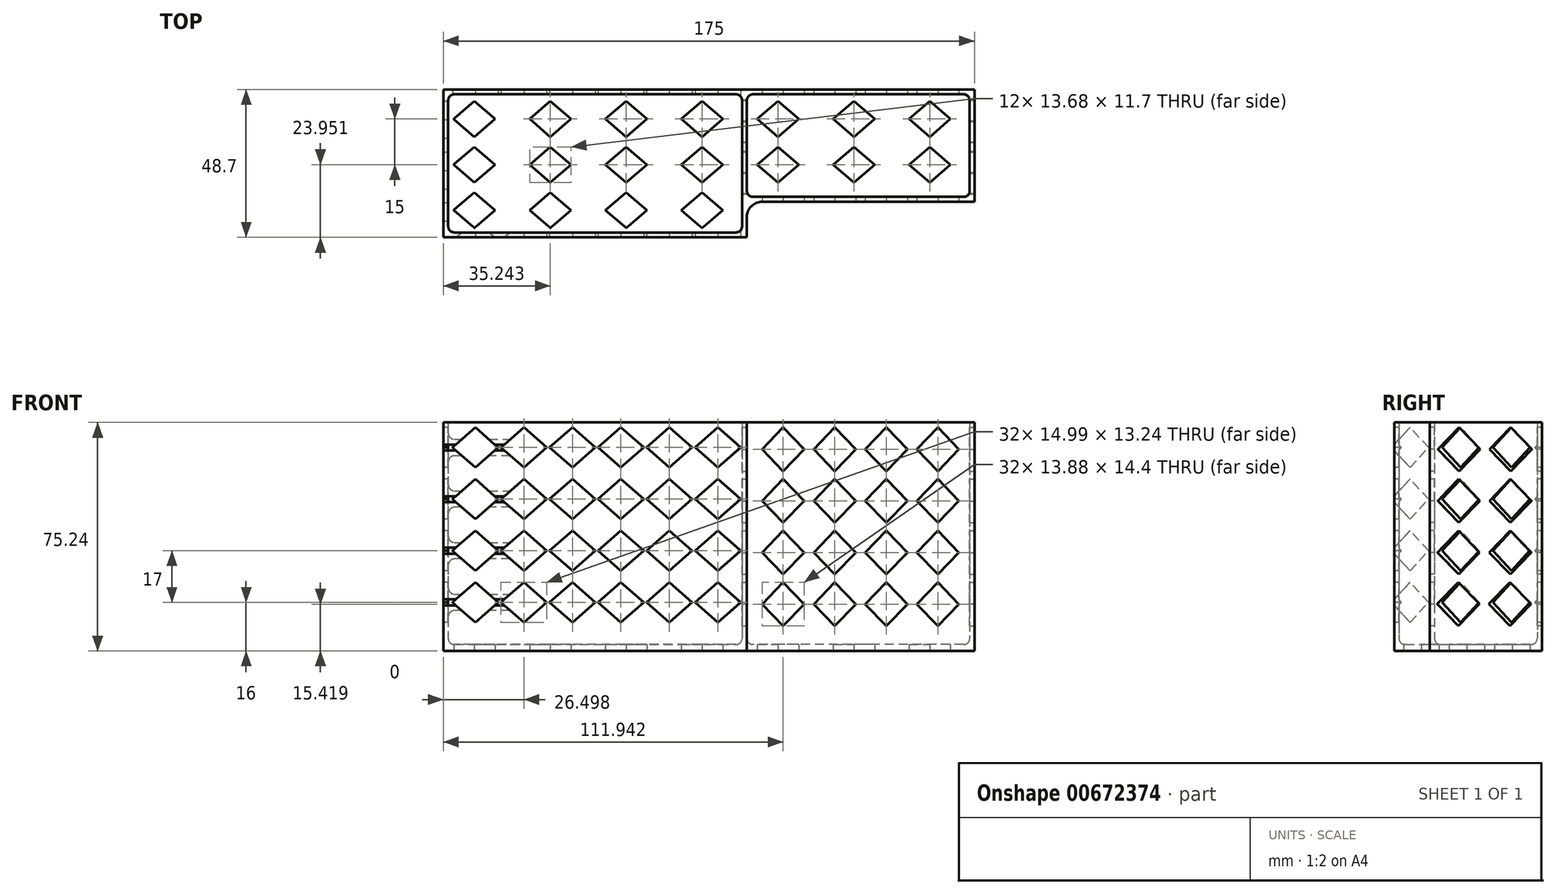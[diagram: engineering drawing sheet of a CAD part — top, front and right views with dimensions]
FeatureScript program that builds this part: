
annotation { "Feature Type Name" : "Feature", "Feature Type Description" : "" }
export const myFeature = defineFeature(function(context is Context, id is Id, definition is map)
    precondition{}
    {
        {
            var Q0;
            Q0=qCreatedBy(makeId("Top.planeOp"),FACE);
            var sketch = newSketch(context, id + "F0", { "sketchPlane" : qUnion([Q0])});
            skLineSegment(sketch, "E0.top", {"start": v(49.36, 40.94) * mm, "end": v(-50.64, 40.94) * mm});
            skPoint(sketch, "E0.middle", {"position": v(0, 0) * mm});
            skLineSegment(sketch, "E1", {"start": v(-49.04, -6.16) * mm, "end": v(47.76, -6.16) * mm});
            skLineSegment(sketch, "E2", {"start": v(-0.64, 40.94) * mm, "end": v(0.56, -22.16) * mm, "construction": true});
            skLineSegment(sketch, "E3.top", {"start": v(47.76, 39.34) * mm, "end": v(-49.04, 39.34) * mm});
            skPoint(sketch, "E3.middle", {"position": v(-0.2, 17.86) * mm});
            skLineSegment(sketch, "E4", {"start": v(47.76, 39.34) * mm, "end": v(47.76, -6.16) * mm});
            skLineSegment(sketch, "E5", {"start": v(-49.04, 39.34) * mm, "end": v(-49.04, -6.16) * mm});
            skLineSegment(sketch, "E6.bottom", {"start": v(49.36, 40.94) * mm, "end": v(124.36, 40.94) * mm});
            skLineSegment(sketch, "E6.top", {"start": v(49.36, 3.94) * mm, "end": v(124.36, 3.94) * mm});
            skLineSegment(sketch, "E6.right", {"start": v(124.36, 40.94) * mm, "end": v(124.36, 3.94) * mm});
            skPoint(sketch, "E7.orphan", {"position": v(-48.1, -7.76) * mm});
            skLineSegment(sketch, "E8", {"start": v(-50.64, -7.76) * mm, "end": v(49.36, -7.76) * mm});
            skLineSegment(sketch, "E9", {"start": v(-50.64, 40.94) * mm, "end": v(-50.64, -7.76) * mm});
            skLineSegment(sketch, "E10", {"start": v(49.36, 3.94) * mm, "end": v(49.36, -7.76) * mm});
            skLineSegment(sketch, "E11.top", {"start": v(49.36, 5.54) * mm, "end": v(122.76, 5.54) * mm});
            skLineSegment(sketch, "E11.right", {"start": v(122.76, 39.34) * mm, "end": v(122.76, 5.54) * mm});
            skPoint(sketch, "E12.orphan", {"position": v(-50.64, -6.16) * mm});
            skPoint(sketch, "E13.orphan", {"position": v(49.36, -6.16) * mm});
            skLineSegment(sketch, "E14", {"start": v(49.36, 39.34) * mm, "end": v(122.76, 39.34) * mm});
            skLineSegment(sketch, "E15", {"start": v(49.36, 39.34) * mm, "end": v(49.36, 5.54) * mm});
            skSolve(sketch);
        }
        {
            var Q0;
            Q0=makeQuery(id+"F0.imprint","IMPRINT",FACE,{"disambiguationData":[TD([[makeQuery(id+"F0.imprint","IMPRINT",EDGE,{"derivedFrom":sQuery(id+"F0.wireOp",EDGE,"E0.top")}),1.0]])]});
            extrude(context, id + "F1", {"entities" : qUnion([Q0]), "depth" : 130 * mm, "offsetDistance" : 25 * mm});
        }
        {
            var Q0;
            Q0=qCreatedBy(makeId("Front.planeOp"),FACE);
            var sketch = newSketch(context, id + "F2", { "sketchPlane" : qUnion([Q0])});
            skLineSegment(sketch, "E16", {"start": v(-50.64, 118) * mm, "end": v(49.36, 118) * mm, "construction": true});
            skLineSegment(sketch, "E17", {"start": v(-40.14, 124.62) * mm, "end": v(-32.65, 118) * mm});
            skLineSegment(sketch, "E18", {"start": v(-32.65, 118) * mm, "end": v(-40.14, 111.38) * mm});
            skLineSegment(sketch, "E19", {"start": v(-40.14, 111.38) * mm, "end": v(-47.64, 118) * mm});
            skLineSegment(sketch, "E20", {"start": v(-47.64, 118) * mm, "end": v(-40.14, 124.62) * mm});
            skLineSegment(sketch, "E21.1.0.0", {"start": v(-31.64, 118) * mm, "end": v(-24.14, 124.62) * mm});
            skLineSegment(sketch, "E21.1.0.1", {"start": v(-24.14, 124.62) * mm, "end": v(-16.65, 118) * mm});
            skLineSegment(sketch, "E21.1.0.2", {"start": v(-16.65, 118) * mm, "end": v(-24.14, 111.38) * mm});
            skLineSegment(sketch, "E21.1.0.3", {"start": v(-24.14, 111.38) * mm, "end": v(-31.64, 118) * mm});
            skLineSegment(sketch, "E21.2.0.0", {"start": v(-15.64, 118) * mm, "end": v(-8.14, 124.62) * mm});
            skLineSegment(sketch, "E21.2.0.1", {"start": v(-8.14, 124.62) * mm, "end": v(-0.65, 118) * mm});
            skLineSegment(sketch, "E21.2.0.2", {"start": v(-0.65, 118) * mm, "end": v(-8.14, 111.38) * mm});
            skLineSegment(sketch, "E21.2.0.3", {"start": v(-8.14, 111.38) * mm, "end": v(-15.64, 118) * mm});
            skLineSegment(sketch, "E21.3.0.0", {"start": v(0.36, 118) * mm, "end": v(7.86, 124.62) * mm});
            skLineSegment(sketch, "E21.3.0.1", {"start": v(7.86, 124.62) * mm, "end": v(15.35, 118) * mm});
            skLineSegment(sketch, "E21.3.0.2", {"start": v(15.35, 118) * mm, "end": v(7.86, 111.38) * mm});
            skLineSegment(sketch, "E21.3.0.3", {"start": v(7.86, 111.38) * mm, "end": v(0.36, 118) * mm});
            skLineSegment(sketch, "E21.4.0.0", {"start": v(16.36, 118) * mm, "end": v(23.86, 124.62) * mm});
            skLineSegment(sketch, "E21.4.0.1", {"start": v(23.86, 124.62) * mm, "end": v(31.35, 118) * mm});
            skLineSegment(sketch, "E21.4.0.2", {"start": v(31.35, 118) * mm, "end": v(23.86, 111.38) * mm});
            skLineSegment(sketch, "E21.4.0.3", {"start": v(23.86, 111.38) * mm, "end": v(16.36, 118) * mm});
            skLineSegment(sketch, "E21.5.0.0", {"start": v(32.36, 118) * mm, "end": v(39.86, 124.62) * mm});
            skLineSegment(sketch, "E21.5.0.1", {"start": v(39.86, 124.62) * mm, "end": v(47.35, 118) * mm});
            skLineSegment(sketch, "E21.5.0.2", {"start": v(47.35, 118) * mm, "end": v(39.86, 111.38) * mm});
            skLineSegment(sketch, "E21.5.0.3", {"start": v(39.86, 111.38) * mm, "end": v(32.36, 118) * mm});
            skLineSegment(sketch, "E21.direction1", {"start": v(-47.64, 118) * mm, "end": v(-31.64, 118) * mm, "construction": true});
            skLineSegment(sketch, "E22.0.1.0", {"start": v(-0.65, 101) * mm, "end": v(-8.14, 94.38) * mm});
            skLineSegment(sketch, "E22.0.1.1", {"start": v(23.86, 107.62) * mm, "end": v(31.35, 101) * mm});
            skLineSegment(sketch, "E22.0.1.2", {"start": v(-47.64, 101) * mm, "end": v(-31.64, 101) * mm, "construction": true});
            skLineSegment(sketch, "E22.0.1.3", {"start": v(31.35, 101) * mm, "end": v(23.86, 94.38) * mm});
            skLineSegment(sketch, "E22.0.1.4", {"start": v(-8.14, 94.38) * mm, "end": v(-15.64, 101) * mm});
            skLineSegment(sketch, "E22.0.1.5", {"start": v(23.86, 94.38) * mm, "end": v(16.36, 101) * mm});
            skLineSegment(sketch, "E22.0.1.6", {"start": v(32.36, 101) * mm, "end": v(39.86, 107.62) * mm});
            skLineSegment(sketch, "E22.0.1.7", {"start": v(-8.14, 107.62) * mm, "end": v(-0.65, 101) * mm});
            skLineSegment(sketch, "E22.0.1.8", {"start": v(-15.64, 101) * mm, "end": v(-8.14, 107.62) * mm});
            skLineSegment(sketch, "E22.0.1.9", {"start": v(-24.14, 94.38) * mm, "end": v(-31.64, 101) * mm});
            skLineSegment(sketch, "E22.0.1.10", {"start": v(39.86, 107.62) * mm, "end": v(47.35, 101) * mm});
            skLineSegment(sketch, "E22.0.1.11", {"start": v(47.35, 101) * mm, "end": v(39.86, 94.38) * mm});
            skLineSegment(sketch, "E22.0.1.12", {"start": v(-16.65, 101) * mm, "end": v(-24.14, 94.38) * mm});
            skLineSegment(sketch, "E22.0.1.13", {"start": v(-47.64, 101) * mm, "end": v(-40.14, 107.62) * mm});
            skLineSegment(sketch, "E22.0.1.14", {"start": v(-31.64, 101) * mm, "end": v(-24.14, 107.62) * mm});
            skLineSegment(sketch, "E22.0.1.15", {"start": v(7.86, 94.38) * mm, "end": v(0.36, 101) * mm});
            skLineSegment(sketch, "E22.0.1.16", {"start": v(39.86, 94.38) * mm, "end": v(32.36, 101) * mm});
            skLineSegment(sketch, "E22.0.1.17", {"start": v(16.36, 101) * mm, "end": v(23.86, 107.62) * mm});
            skLineSegment(sketch, "E22.0.1.18", {"start": v(0.36, 101) * mm, "end": v(7.86, 107.62) * mm});
            skLineSegment(sketch, "E22.0.1.19", {"start": v(7.86, 107.62) * mm, "end": v(15.35, 101) * mm});
            skLineSegment(sketch, "E22.0.1.20", {"start": v(15.35, 101) * mm, "end": v(7.86, 94.38) * mm});
            skLineSegment(sketch, "E22.0.1.21", {"start": v(-40.14, 107.62) * mm, "end": v(-32.65, 101) * mm});
            skLineSegment(sketch, "E22.0.1.22", {"start": v(-32.65, 101) * mm, "end": v(-40.14, 94.38) * mm});
            skLineSegment(sketch, "E22.0.1.23", {"start": v(-40.14, 94.38) * mm, "end": v(-47.64, 101) * mm});
            skLineSegment(sketch, "E22.0.1.24", {"start": v(-24.14, 107.62) * mm, "end": v(-16.65, 101) * mm});
            skLineSegment(sketch, "E22.0.2.0", {"start": v(-0.65, 84) * mm, "end": v(-8.14, 77.38) * mm});
            skLineSegment(sketch, "E22.0.2.1", {"start": v(23.86, 90.62) * mm, "end": v(31.35, 84) * mm});
            skLineSegment(sketch, "E22.0.2.2", {"start": v(-47.64, 84) * mm, "end": v(-31.64, 84) * mm, "construction": true});
            skLineSegment(sketch, "E22.0.2.3", {"start": v(31.35, 84) * mm, "end": v(23.86, 77.38) * mm});
            skLineSegment(sketch, "E22.0.2.4", {"start": v(-8.14, 77.38) * mm, "end": v(-15.64, 84) * mm});
            skLineSegment(sketch, "E22.0.2.5", {"start": v(23.86, 77.38) * mm, "end": v(16.36, 84) * mm});
            skLineSegment(sketch, "E22.0.2.6", {"start": v(32.36, 84) * mm, "end": v(39.86, 90.62) * mm});
            skLineSegment(sketch, "E22.0.2.7", {"start": v(-8.14, 90.62) * mm, "end": v(-0.65, 84) * mm});
            skLineSegment(sketch, "E22.0.2.8", {"start": v(-15.64, 84) * mm, "end": v(-8.14, 90.62) * mm});
            skLineSegment(sketch, "E22.0.2.9", {"start": v(-24.14, 77.38) * mm, "end": v(-31.64, 84) * mm});
            skLineSegment(sketch, "E22.0.2.10", {"start": v(39.86, 90.62) * mm, "end": v(47.35, 84) * mm});
            skLineSegment(sketch, "E22.0.2.11", {"start": v(47.35, 84) * mm, "end": v(39.86, 77.38) * mm});
            skLineSegment(sketch, "E22.0.2.12", {"start": v(-16.65, 84) * mm, "end": v(-24.14, 77.38) * mm});
            skLineSegment(sketch, "E22.0.2.13", {"start": v(-47.64, 84) * mm, "end": v(-40.14, 90.62) * mm});
            skLineSegment(sketch, "E22.0.2.14", {"start": v(-31.64, 84) * mm, "end": v(-24.14, 90.62) * mm});
            skLineSegment(sketch, "E22.0.2.15", {"start": v(7.86, 77.38) * mm, "end": v(0.36, 84) * mm});
            skLineSegment(sketch, "E22.0.2.16", {"start": v(39.86, 77.38) * mm, "end": v(32.36, 84) * mm});
            skLineSegment(sketch, "E22.0.2.17", {"start": v(16.36, 84) * mm, "end": v(23.86, 90.62) * mm});
            skLineSegment(sketch, "E22.0.2.18", {"start": v(0.36, 84) * mm, "end": v(7.86, 90.62) * mm});
            skLineSegment(sketch, "E22.0.2.19", {"start": v(7.86, 90.62) * mm, "end": v(15.35, 84) * mm});
            skLineSegment(sketch, "E22.0.2.20", {"start": v(15.35, 84) * mm, "end": v(7.86, 77.38) * mm});
            skLineSegment(sketch, "E22.0.2.21", {"start": v(-40.14, 90.62) * mm, "end": v(-32.65, 84) * mm});
            skLineSegment(sketch, "E22.0.2.22", {"start": v(-32.65, 84) * mm, "end": v(-40.14, 77.38) * mm});
            skLineSegment(sketch, "E22.0.2.23", {"start": v(-40.14, 77.38) * mm, "end": v(-47.64, 84) * mm});
            skLineSegment(sketch, "E22.0.2.24", {"start": v(-24.14, 90.62) * mm, "end": v(-16.65, 84) * mm});
            skLineSegment(sketch, "E22.0.3.0", {"start": v(-0.65, 67) * mm, "end": v(-8.14, 60.38) * mm});
            skLineSegment(sketch, "E22.0.3.1", {"start": v(23.86, 73.62) * mm, "end": v(31.35, 67) * mm});
            skLineSegment(sketch, "E22.0.3.2", {"start": v(-47.64, 67) * mm, "end": v(-31.64, 67) * mm, "construction": true});
            skLineSegment(sketch, "E22.0.3.3", {"start": v(31.35, 67) * mm, "end": v(23.86, 60.38) * mm});
            skLineSegment(sketch, "E22.0.3.4", {"start": v(-8.14, 60.38) * mm, "end": v(-15.64, 67) * mm});
            skLineSegment(sketch, "E22.0.3.5", {"start": v(23.86, 60.38) * mm, "end": v(16.36, 67) * mm});
            skLineSegment(sketch, "E22.0.3.6", {"start": v(32.36, 67) * mm, "end": v(39.86, 73.62) * mm});
            skLineSegment(sketch, "E22.0.3.7", {"start": v(-8.14, 73.62) * mm, "end": v(-0.65, 67) * mm});
            skLineSegment(sketch, "E22.0.3.8", {"start": v(-15.64, 67) * mm, "end": v(-8.14, 73.62) * mm});
            skLineSegment(sketch, "E22.0.3.9", {"start": v(-24.14, 60.38) * mm, "end": v(-31.64, 67) * mm});
            skLineSegment(sketch, "E22.0.3.10", {"start": v(39.86, 73.62) * mm, "end": v(47.35, 67) * mm});
            skLineSegment(sketch, "E22.0.3.11", {"start": v(47.35, 67) * mm, "end": v(39.86, 60.38) * mm});
            skLineSegment(sketch, "E22.0.3.12", {"start": v(-16.65, 67) * mm, "end": v(-24.14, 60.38) * mm});
            skLineSegment(sketch, "E22.0.3.13", {"start": v(-47.64, 67) * mm, "end": v(-40.14, 73.62) * mm});
            skLineSegment(sketch, "E22.0.3.14", {"start": v(-31.64, 67) * mm, "end": v(-24.14, 73.62) * mm});
            skLineSegment(sketch, "E22.0.3.15", {"start": v(7.86, 60.38) * mm, "end": v(0.36, 67) * mm});
            skLineSegment(sketch, "E22.0.3.16", {"start": v(39.86, 60.38) * mm, "end": v(32.36, 67) * mm});
            skLineSegment(sketch, "E22.0.3.17", {"start": v(16.36, 67) * mm, "end": v(23.86, 73.62) * mm});
            skLineSegment(sketch, "E22.0.3.18", {"start": v(0.36, 67) * mm, "end": v(7.86, 73.62) * mm});
            skLineSegment(sketch, "E22.0.3.19", {"start": v(7.86, 73.62) * mm, "end": v(15.35, 67) * mm});
            skLineSegment(sketch, "E22.0.3.20", {"start": v(15.35, 67) * mm, "end": v(7.86, 60.38) * mm});
            skLineSegment(sketch, "E22.0.3.21", {"start": v(-40.14, 73.62) * mm, "end": v(-32.65, 67) * mm});
            skLineSegment(sketch, "E22.0.3.22", {"start": v(-32.65, 67) * mm, "end": v(-40.14, 60.38) * mm});
            skLineSegment(sketch, "E22.0.3.23", {"start": v(-40.14, 60.38) * mm, "end": v(-47.64, 67) * mm});
            skLineSegment(sketch, "E22.0.3.24", {"start": v(-24.14, 73.62) * mm, "end": v(-16.65, 67) * mm});
            skLineSegment(sketch, "E22.0.4.0", {"start": v(-0.65, 50) * mm, "end": v(-8.14, 43.38) * mm});
            skLineSegment(sketch, "E22.0.4.1", {"start": v(23.86, 56.62) * mm, "end": v(31.35, 50) * mm});
            skLineSegment(sketch, "E22.0.4.2", {"start": v(-47.64, 50) * mm, "end": v(-31.64, 50) * mm, "construction": true});
            skLineSegment(sketch, "E22.0.4.3", {"start": v(31.35, 50) * mm, "end": v(23.86, 43.38) * mm});
            skLineSegment(sketch, "E22.0.4.4", {"start": v(-8.14, 43.38) * mm, "end": v(-15.64, 50) * mm});
            skLineSegment(sketch, "E22.0.4.5", {"start": v(23.86, 43.38) * mm, "end": v(16.36, 50) * mm});
            skLineSegment(sketch, "E22.0.4.6", {"start": v(32.36, 50) * mm, "end": v(39.86, 56.62) * mm});
            skLineSegment(sketch, "E22.0.4.7", {"start": v(-8.14, 56.62) * mm, "end": v(-0.65, 50) * mm});
            skLineSegment(sketch, "E22.0.4.8", {"start": v(-15.64, 50) * mm, "end": v(-8.14, 56.62) * mm});
            skLineSegment(sketch, "E22.0.4.9", {"start": v(-24.14, 43.38) * mm, "end": v(-31.64, 50) * mm});
            skLineSegment(sketch, "E22.0.4.10", {"start": v(39.86, 56.62) * mm, "end": v(47.35, 50) * mm});
            skLineSegment(sketch, "E22.0.4.11", {"start": v(47.35, 50) * mm, "end": v(39.86, 43.38) * mm});
            skLineSegment(sketch, "E22.0.4.12", {"start": v(-16.65, 50) * mm, "end": v(-24.14, 43.38) * mm});
            skLineSegment(sketch, "E22.0.4.13", {"start": v(-47.64, 50) * mm, "end": v(-40.14, 56.62) * mm});
            skLineSegment(sketch, "E22.0.4.14", {"start": v(-31.64, 50) * mm, "end": v(-24.14, 56.62) * mm});
            skLineSegment(sketch, "E22.0.4.15", {"start": v(7.86, 43.38) * mm, "end": v(0.36, 50) * mm});
            skLineSegment(sketch, "E22.0.4.16", {"start": v(39.86, 43.38) * mm, "end": v(32.36, 50) * mm});
            skLineSegment(sketch, "E22.0.4.17", {"start": v(16.36, 50) * mm, "end": v(23.86, 56.62) * mm});
            skLineSegment(sketch, "E22.0.4.18", {"start": v(0.36, 50) * mm, "end": v(7.86, 56.62) * mm});
            skLineSegment(sketch, "E22.0.4.19", {"start": v(7.86, 56.62) * mm, "end": v(15.35, 50) * mm});
            skLineSegment(sketch, "E22.0.4.20", {"start": v(15.35, 50) * mm, "end": v(7.86, 43.38) * mm});
            skLineSegment(sketch, "E22.0.4.21", {"start": v(-40.14, 56.62) * mm, "end": v(-32.65, 50) * mm});
            skLineSegment(sketch, "E22.0.4.22", {"start": v(-32.65, 50) * mm, "end": v(-40.14, 43.38) * mm});
            skLineSegment(sketch, "E22.0.4.23", {"start": v(-40.14, 43.38) * mm, "end": v(-47.64, 50) * mm});
            skLineSegment(sketch, "E22.0.4.24", {"start": v(-24.14, 56.62) * mm, "end": v(-16.65, 50) * mm});
            skLineSegment(sketch, "E22.0.5.0", {"start": v(-0.65, 33) * mm, "end": v(-8.14, 26.38) * mm});
            skLineSegment(sketch, "E22.0.5.1", {"start": v(23.86, 39.62) * mm, "end": v(31.35, 33) * mm});
            skLineSegment(sketch, "E22.0.5.2", {"start": v(-47.64, 33) * mm, "end": v(-31.64, 33) * mm, "construction": true});
            skLineSegment(sketch, "E22.0.5.3", {"start": v(31.35, 33) * mm, "end": v(23.86, 26.38) * mm});
            skLineSegment(sketch, "E22.0.5.4", {"start": v(-8.14, 26.38) * mm, "end": v(-15.64, 33) * mm});
            skLineSegment(sketch, "E22.0.5.5", {"start": v(23.86, 26.38) * mm, "end": v(16.36, 33) * mm});
            skLineSegment(sketch, "E22.0.5.6", {"start": v(32.36, 33) * mm, "end": v(39.86, 39.62) * mm});
            skLineSegment(sketch, "E22.0.5.7", {"start": v(-8.14, 39.62) * mm, "end": v(-0.65, 33) * mm});
            skLineSegment(sketch, "E22.0.5.8", {"start": v(-15.64, 33) * mm, "end": v(-8.14, 39.62) * mm});
            skLineSegment(sketch, "E22.0.5.9", {"start": v(-24.14, 26.38) * mm, "end": v(-31.64, 33) * mm});
            skLineSegment(sketch, "E22.0.5.10", {"start": v(39.86, 39.62) * mm, "end": v(47.35, 33) * mm});
            skLineSegment(sketch, "E22.0.5.11", {"start": v(47.35, 33) * mm, "end": v(39.86, 26.38) * mm});
            skLineSegment(sketch, "E22.0.5.12", {"start": v(-16.65, 33) * mm, "end": v(-24.14, 26.38) * mm});
            skLineSegment(sketch, "E22.0.5.13", {"start": v(-47.64, 33) * mm, "end": v(-40.14, 39.62) * mm});
            skLineSegment(sketch, "E22.0.5.14", {"start": v(-31.64, 33) * mm, "end": v(-24.14, 39.62) * mm});
            skLineSegment(sketch, "E22.0.5.15", {"start": v(7.86, 26.38) * mm, "end": v(0.36, 33) * mm});
            skLineSegment(sketch, "E22.0.5.16", {"start": v(39.86, 26.38) * mm, "end": v(32.36, 33) * mm});
            skLineSegment(sketch, "E22.0.5.17", {"start": v(16.36, 33) * mm, "end": v(23.86, 39.62) * mm});
            skLineSegment(sketch, "E22.0.5.18", {"start": v(0.36, 33) * mm, "end": v(7.86, 39.62) * mm});
            skLineSegment(sketch, "E22.0.5.19", {"start": v(7.86, 39.62) * mm, "end": v(15.35, 33) * mm});
            skLineSegment(sketch, "E22.0.5.20", {"start": v(15.35, 33) * mm, "end": v(7.86, 26.38) * mm});
            skLineSegment(sketch, "E22.0.5.21", {"start": v(-40.14, 39.62) * mm, "end": v(-32.65, 33) * mm});
            skLineSegment(sketch, "E22.0.5.22", {"start": v(-32.65, 33) * mm, "end": v(-40.14, 26.38) * mm});
            skLineSegment(sketch, "E22.0.5.23", {"start": v(-40.14, 26.38) * mm, "end": v(-47.64, 33) * mm});
            skLineSegment(sketch, "E22.0.5.24", {"start": v(-24.14, 39.62) * mm, "end": v(-16.65, 33) * mm});
            skLineSegment(sketch, "E22.0.6.0", {"start": v(-0.65, 16) * mm, "end": v(-8.14, 9.38) * mm});
            skLineSegment(sketch, "E22.0.6.1", {"start": v(23.86, 22.62) * mm, "end": v(31.35, 16) * mm});
            skLineSegment(sketch, "E22.0.6.2", {"start": v(-47.64, 16) * mm, "end": v(-31.64, 16) * mm, "construction": true});
            skLineSegment(sketch, "E22.0.6.3", {"start": v(31.35, 16) * mm, "end": v(23.86, 9.38) * mm});
            skLineSegment(sketch, "E22.0.6.4", {"start": v(-8.14, 9.38) * mm, "end": v(-15.64, 16) * mm});
            skLineSegment(sketch, "E22.0.6.5", {"start": v(23.86, 9.38) * mm, "end": v(16.36, 16) * mm});
            skLineSegment(sketch, "E22.0.6.6", {"start": v(32.36, 16) * mm, "end": v(39.86, 22.62) * mm});
            skLineSegment(sketch, "E22.0.6.7", {"start": v(-8.14, 22.62) * mm, "end": v(-0.65, 16) * mm});
            skLineSegment(sketch, "E22.0.6.8", {"start": v(-15.64, 16) * mm, "end": v(-8.14, 22.62) * mm});
            skLineSegment(sketch, "E22.0.6.9", {"start": v(-24.14, 9.38) * mm, "end": v(-31.64, 16) * mm});
            skLineSegment(sketch, "E22.0.6.10", {"start": v(39.86, 22.62) * mm, "end": v(47.35, 16) * mm});
            skLineSegment(sketch, "E22.0.6.11", {"start": v(47.35, 16) * mm, "end": v(39.86, 9.38) * mm});
            skLineSegment(sketch, "E22.0.6.12", {"start": v(-16.65, 16) * mm, "end": v(-24.14, 9.38) * mm});
            skLineSegment(sketch, "E22.0.6.13", {"start": v(-47.64, 16) * mm, "end": v(-40.14, 22.62) * mm});
            skLineSegment(sketch, "E22.0.6.14", {"start": v(-31.64, 16) * mm, "end": v(-24.14, 22.62) * mm});
            skLineSegment(sketch, "E22.0.6.15", {"start": v(7.86, 9.38) * mm, "end": v(0.36, 16) * mm});
            skLineSegment(sketch, "E22.0.6.16", {"start": v(39.86, 9.38) * mm, "end": v(32.36, 16) * mm});
            skLineSegment(sketch, "E22.0.6.17", {"start": v(16.36, 16) * mm, "end": v(23.86, 22.62) * mm});
            skLineSegment(sketch, "E22.0.6.18", {"start": v(0.36, 16) * mm, "end": v(7.86, 22.62) * mm});
            skLineSegment(sketch, "E22.0.6.19", {"start": v(7.86, 22.62) * mm, "end": v(15.35, 16) * mm});
            skLineSegment(sketch, "E22.0.6.20", {"start": v(15.35, 16) * mm, "end": v(7.86, 9.38) * mm});
            skLineSegment(sketch, "E22.0.6.21", {"start": v(-40.14, 22.62) * mm, "end": v(-32.65, 16) * mm});
            skLineSegment(sketch, "E22.0.6.22", {"start": v(-32.65, 16) * mm, "end": v(-40.14, 9.38) * mm});
            skLineSegment(sketch, "E22.0.6.23", {"start": v(-40.14, 9.38) * mm, "end": v(-47.64, 16) * mm});
            skLineSegment(sketch, "E22.0.6.24", {"start": v(-24.14, 22.62) * mm, "end": v(-16.65, 16) * mm});
            skLineSegment(sketch, "E22.direction1", {"start": v(-40.14, 111.38) * mm, "end": v(-15.14, 111.38) * mm, "construction": true});
            skLineSegment(sketch, "E22.direction2", {"start": v(-40.14, 111.38) * mm, "end": v(-40.14, 94.38) * mm, "construction": true});
            skSolve(sketch);
        }
        {
            var Q0;
            Q0=makeQuery(id+"F1.opExtrude","SWEPT_FACE",FACE,{"disambiguationData":[OSD([sQuery(id+"F0.wireOp",EDGE,"E6.top")])]});
            var sketch = newSketch(context, id + "F3", { "sketchPlane" : qUnion([Q0])});
            skLineSegment(sketch, "E23", {"start": v(49.36, 117.42) * mm, "end": v(124.36, 117.42) * mm, "construction": true});
            skLineSegment(sketch, "E24", {"start": v(61.3, 124.62) * mm, "end": v(68.24, 117.42) * mm});
            skLineSegment(sketch, "E25", {"start": v(68.24, 117.42) * mm, "end": v(61.3, 110.22) * mm});
            skLineSegment(sketch, "E26", {"start": v(61.3, 110.22) * mm, "end": v(54.36, 117.42) * mm});
            skLineSegment(sketch, "E27", {"start": v(54.36, 117.42) * mm, "end": v(61.3, 124.62) * mm});
            skLineSegment(sketch, "E28.0.1.0", {"start": v(54.36, 100.42) * mm, "end": v(61.3, 107.62) * mm});
            skLineSegment(sketch, "E28.0.1.1", {"start": v(61.3, 107.62) * mm, "end": v(68.24, 100.42) * mm});
            skLineSegment(sketch, "E28.0.1.2", {"start": v(68.24, 100.42) * mm, "end": v(61.3, 93.22) * mm});
            skLineSegment(sketch, "E28.0.1.3", {"start": v(61.3, 93.22) * mm, "end": v(54.36, 100.42) * mm});
            skLineSegment(sketch, "E28.0.2.0", {"start": v(54.36, 83.42) * mm, "end": v(61.3, 90.62) * mm});
            skLineSegment(sketch, "E28.0.2.1", {"start": v(61.3, 90.62) * mm, "end": v(68.24, 83.42) * mm});
            skLineSegment(sketch, "E28.0.2.2", {"start": v(68.24, 83.42) * mm, "end": v(61.3, 76.22) * mm});
            skLineSegment(sketch, "E28.0.2.3", {"start": v(61.3, 76.22) * mm, "end": v(54.36, 83.42) * mm});
            skLineSegment(sketch, "E28.0.3.0", {"start": v(54.36, 66.42) * mm, "end": v(61.3, 73.62) * mm});
            skLineSegment(sketch, "E28.0.3.1", {"start": v(61.3, 73.62) * mm, "end": v(68.24, 66.42) * mm});
            skLineSegment(sketch, "E28.0.3.2", {"start": v(68.24, 66.42) * mm, "end": v(61.3, 59.22) * mm});
            skLineSegment(sketch, "E28.0.3.3", {"start": v(61.3, 59.22) * mm, "end": v(54.36, 66.42) * mm});
            skLineSegment(sketch, "E28.0.4.0", {"start": v(54.36, 49.42) * mm, "end": v(61.3, 56.62) * mm});
            skLineSegment(sketch, "E28.0.4.1", {"start": v(61.3, 56.62) * mm, "end": v(68.24, 49.42) * mm});
            skLineSegment(sketch, "E28.0.4.2", {"start": v(68.24, 49.42) * mm, "end": v(61.3, 42.22) * mm});
            skLineSegment(sketch, "E28.0.4.3", {"start": v(61.3, 42.22) * mm, "end": v(54.36, 49.42) * mm});
            skLineSegment(sketch, "E28.0.5.0", {"start": v(54.36, 32.42) * mm, "end": v(61.3, 39.62) * mm});
            skLineSegment(sketch, "E28.0.5.1", {"start": v(61.3, 39.62) * mm, "end": v(68.24, 32.42) * mm});
            skLineSegment(sketch, "E28.0.5.2", {"start": v(68.24, 32.42) * mm, "end": v(61.3, 25.22) * mm});
            skLineSegment(sketch, "E28.0.5.3", {"start": v(61.3, 25.22) * mm, "end": v(54.36, 32.42) * mm});
            skLineSegment(sketch, "E28.0.6.0", {"start": v(54.36, 15.42) * mm, "end": v(61.3, 22.62) * mm});
            skLineSegment(sketch, "E28.0.6.1", {"start": v(61.3, 22.62) * mm, "end": v(68.24, 15.42) * mm});
            skLineSegment(sketch, "E28.0.6.2", {"start": v(68.24, 15.42) * mm, "end": v(61.3, 8.22) * mm});
            skLineSegment(sketch, "E28.0.6.3", {"start": v(61.3, 8.22) * mm, "end": v(54.36, 15.42) * mm});
            skLineSegment(sketch, "E28.1.0.0", {"start": v(71.36, 117.42) * mm, "end": v(78.3, 124.62) * mm});
            skLineSegment(sketch, "E28.1.0.1", {"start": v(78.3, 124.62) * mm, "end": v(85.24, 117.42) * mm});
            skLineSegment(sketch, "E28.1.0.2", {"start": v(85.24, 117.42) * mm, "end": v(78.3, 110.22) * mm});
            skLineSegment(sketch, "E28.1.0.3", {"start": v(78.3, 110.22) * mm, "end": v(71.36, 117.42) * mm});
            skLineSegment(sketch, "E28.1.1.0", {"start": v(71.36, 100.42) * mm, "end": v(78.3, 107.62) * mm});
            skLineSegment(sketch, "E28.1.1.1", {"start": v(78.3, 107.62) * mm, "end": v(85.24, 100.42) * mm});
            skLineSegment(sketch, "E28.1.1.2", {"start": v(85.24, 100.42) * mm, "end": v(78.3, 93.22) * mm});
            skLineSegment(sketch, "E28.1.1.3", {"start": v(78.3, 93.22) * mm, "end": v(71.36, 100.42) * mm});
            skLineSegment(sketch, "E28.1.2.0", {"start": v(71.36, 83.42) * mm, "end": v(78.3, 90.62) * mm});
            skLineSegment(sketch, "E28.1.2.1", {"start": v(78.3, 90.62) * mm, "end": v(85.24, 83.42) * mm});
            skLineSegment(sketch, "E28.1.2.2", {"start": v(85.24, 83.42) * mm, "end": v(78.3, 76.22) * mm});
            skLineSegment(sketch, "E28.1.2.3", {"start": v(78.3, 76.22) * mm, "end": v(71.36, 83.42) * mm});
            skLineSegment(sketch, "E28.1.3.0", {"start": v(71.36, 66.42) * mm, "end": v(78.3, 73.62) * mm});
            skLineSegment(sketch, "E28.1.3.1", {"start": v(78.3, 73.62) * mm, "end": v(85.24, 66.42) * mm});
            skLineSegment(sketch, "E28.1.3.2", {"start": v(85.24, 66.42) * mm, "end": v(78.3, 59.22) * mm});
            skLineSegment(sketch, "E28.1.3.3", {"start": v(78.3, 59.22) * mm, "end": v(71.36, 66.42) * mm});
            skLineSegment(sketch, "E28.1.4.0", {"start": v(71.36, 49.42) * mm, "end": v(78.3, 56.62) * mm});
            skLineSegment(sketch, "E28.1.4.1", {"start": v(78.3, 56.62) * mm, "end": v(85.24, 49.42) * mm});
            skLineSegment(sketch, "E28.1.4.2", {"start": v(85.24, 49.42) * mm, "end": v(78.3, 42.22) * mm});
            skLineSegment(sketch, "E28.1.4.3", {"start": v(78.3, 42.22) * mm, "end": v(71.36, 49.42) * mm});
            skLineSegment(sketch, "E28.1.5.0", {"start": v(71.36, 32.42) * mm, "end": v(78.3, 39.62) * mm});
            skLineSegment(sketch, "E28.1.5.1", {"start": v(78.3, 39.62) * mm, "end": v(85.24, 32.42) * mm});
            skLineSegment(sketch, "E28.1.5.2", {"start": v(85.24, 32.42) * mm, "end": v(78.3, 25.22) * mm});
            skLineSegment(sketch, "E28.1.5.3", {"start": v(78.3, 25.22) * mm, "end": v(71.36, 32.42) * mm});
            skLineSegment(sketch, "E28.1.6.0", {"start": v(71.36, 15.42) * mm, "end": v(78.3, 22.62) * mm});
            skLineSegment(sketch, "E28.1.6.1", {"start": v(78.3, 22.62) * mm, "end": v(85.24, 15.42) * mm});
            skLineSegment(sketch, "E28.1.6.2", {"start": v(85.24, 15.42) * mm, "end": v(78.3, 8.22) * mm});
            skLineSegment(sketch, "E28.1.6.3", {"start": v(78.3, 8.22) * mm, "end": v(71.36, 15.42) * mm});
            skLineSegment(sketch, "E28.2.0.0", {"start": v(88.36, 117.42) * mm, "end": v(95.3, 124.62) * mm});
            skLineSegment(sketch, "E28.2.0.1", {"start": v(95.3, 124.62) * mm, "end": v(102.24, 117.42) * mm});
            skLineSegment(sketch, "E28.2.0.2", {"start": v(102.24, 117.42) * mm, "end": v(95.3, 110.22) * mm});
            skLineSegment(sketch, "E28.2.0.3", {"start": v(95.3, 110.22) * mm, "end": v(88.36, 117.42) * mm});
            skLineSegment(sketch, "E28.2.1.0", {"start": v(88.36, 100.42) * mm, "end": v(95.3, 107.62) * mm});
            skLineSegment(sketch, "E28.2.1.1", {"start": v(95.3, 107.62) * mm, "end": v(102.24, 100.42) * mm});
            skLineSegment(sketch, "E28.2.1.2", {"start": v(102.24, 100.42) * mm, "end": v(95.3, 93.22) * mm});
            skLineSegment(sketch, "E28.2.1.3", {"start": v(95.3, 93.22) * mm, "end": v(88.36, 100.42) * mm});
            skLineSegment(sketch, "E28.2.2.0", {"start": v(88.36, 83.42) * mm, "end": v(95.3, 90.62) * mm});
            skLineSegment(sketch, "E28.2.2.1", {"start": v(95.3, 90.62) * mm, "end": v(102.24, 83.42) * mm});
            skLineSegment(sketch, "E28.2.2.2", {"start": v(102.24, 83.42) * mm, "end": v(95.3, 76.22) * mm});
            skLineSegment(sketch, "E28.2.2.3", {"start": v(95.3, 76.22) * mm, "end": v(88.36, 83.42) * mm});
            skLineSegment(sketch, "E28.2.3.0", {"start": v(88.36, 66.42) * mm, "end": v(95.3, 73.62) * mm});
            skLineSegment(sketch, "E28.2.3.1", {"start": v(95.3, 73.62) * mm, "end": v(102.24, 66.42) * mm});
            skLineSegment(sketch, "E28.2.3.2", {"start": v(102.24, 66.42) * mm, "end": v(95.3, 59.22) * mm});
            skLineSegment(sketch, "E28.2.3.3", {"start": v(95.3, 59.22) * mm, "end": v(88.36, 66.42) * mm});
            skLineSegment(sketch, "E28.2.4.0", {"start": v(88.36, 49.42) * mm, "end": v(95.3, 56.62) * mm});
            skLineSegment(sketch, "E28.2.4.1", {"start": v(95.3, 56.62) * mm, "end": v(102.24, 49.42) * mm});
            skLineSegment(sketch, "E28.2.4.2", {"start": v(102.24, 49.42) * mm, "end": v(95.3, 42.22) * mm});
            skLineSegment(sketch, "E28.2.4.3", {"start": v(95.3, 42.22) * mm, "end": v(88.36, 49.42) * mm});
            skLineSegment(sketch, "E28.2.5.0", {"start": v(88.36, 32.42) * mm, "end": v(95.3, 39.62) * mm});
            skLineSegment(sketch, "E28.2.5.1", {"start": v(95.3, 39.62) * mm, "end": v(102.24, 32.42) * mm});
            skLineSegment(sketch, "E28.2.5.2", {"start": v(102.24, 32.42) * mm, "end": v(95.3, 25.22) * mm});
            skLineSegment(sketch, "E28.2.5.3", {"start": v(95.3, 25.22) * mm, "end": v(88.36, 32.42) * mm});
            skLineSegment(sketch, "E28.2.6.0", {"start": v(88.36, 15.42) * mm, "end": v(95.3, 22.62) * mm});
            skLineSegment(sketch, "E28.2.6.1", {"start": v(95.3, 22.62) * mm, "end": v(102.24, 15.42) * mm});
            skLineSegment(sketch, "E28.2.6.2", {"start": v(102.24, 15.42) * mm, "end": v(95.3, 8.22) * mm});
            skLineSegment(sketch, "E28.2.6.3", {"start": v(95.3, 8.22) * mm, "end": v(88.36, 15.42) * mm});
            skLineSegment(sketch, "E28.3.0.0", {"start": v(105.36, 117.42) * mm, "end": v(112.3, 124.62) * mm});
            skLineSegment(sketch, "E28.3.0.1", {"start": v(112.3, 124.62) * mm, "end": v(119.24, 117.42) * mm});
            skLineSegment(sketch, "E28.3.0.2", {"start": v(119.24, 117.42) * mm, "end": v(112.3, 110.22) * mm});
            skLineSegment(sketch, "E28.3.0.3", {"start": v(112.3, 110.22) * mm, "end": v(105.36, 117.42) * mm});
            skLineSegment(sketch, "E28.3.1.0", {"start": v(105.36, 100.42) * mm, "end": v(112.3, 107.62) * mm});
            skLineSegment(sketch, "E28.3.1.1", {"start": v(112.3, 107.62) * mm, "end": v(119.24, 100.42) * mm});
            skLineSegment(sketch, "E28.3.1.2", {"start": v(119.24, 100.42) * mm, "end": v(112.3, 93.22) * mm});
            skLineSegment(sketch, "E28.3.1.3", {"start": v(112.3, 93.22) * mm, "end": v(105.36, 100.42) * mm});
            skLineSegment(sketch, "E28.3.2.0", {"start": v(105.36, 83.42) * mm, "end": v(112.3, 90.62) * mm});
            skLineSegment(sketch, "E28.3.2.1", {"start": v(112.3, 90.62) * mm, "end": v(119.24, 83.42) * mm});
            skLineSegment(sketch, "E28.3.2.2", {"start": v(119.24, 83.42) * mm, "end": v(112.3, 76.22) * mm});
            skLineSegment(sketch, "E28.3.2.3", {"start": v(112.3, 76.22) * mm, "end": v(105.36, 83.42) * mm});
            skLineSegment(sketch, "E28.3.3.0", {"start": v(105.36, 66.42) * mm, "end": v(112.3, 73.62) * mm});
            skLineSegment(sketch, "E28.3.3.1", {"start": v(112.3, 73.62) * mm, "end": v(119.24, 66.42) * mm});
            skLineSegment(sketch, "E28.3.3.2", {"start": v(119.24, 66.42) * mm, "end": v(112.3, 59.22) * mm});
            skLineSegment(sketch, "E28.3.3.3", {"start": v(112.3, 59.22) * mm, "end": v(105.36, 66.42) * mm});
            skLineSegment(sketch, "E28.3.4.0", {"start": v(105.36, 49.42) * mm, "end": v(112.3, 56.62) * mm});
            skLineSegment(sketch, "E28.3.4.1", {"start": v(112.3, 56.62) * mm, "end": v(119.24, 49.42) * mm});
            skLineSegment(sketch, "E28.3.4.2", {"start": v(119.24, 49.42) * mm, "end": v(112.3, 42.22) * mm});
            skLineSegment(sketch, "E28.3.4.3", {"start": v(112.3, 42.22) * mm, "end": v(105.36, 49.42) * mm});
            skLineSegment(sketch, "E28.3.5.0", {"start": v(105.36, 32.42) * mm, "end": v(112.3, 39.62) * mm});
            skLineSegment(sketch, "E28.3.5.1", {"start": v(112.3, 39.62) * mm, "end": v(119.24, 32.42) * mm});
            skLineSegment(sketch, "E28.3.5.2", {"start": v(119.24, 32.42) * mm, "end": v(112.3, 25.22) * mm});
            skLineSegment(sketch, "E28.3.5.3", {"start": v(112.3, 25.22) * mm, "end": v(105.36, 32.42) * mm});
            skLineSegment(sketch, "E28.3.6.0", {"start": v(105.36, 15.42) * mm, "end": v(112.3, 22.62) * mm});
            skLineSegment(sketch, "E28.3.6.1", {"start": v(112.3, 22.62) * mm, "end": v(119.24, 15.42) * mm});
            skLineSegment(sketch, "E28.3.6.2", {"start": v(119.24, 15.42) * mm, "end": v(112.3, 8.22) * mm});
            skLineSegment(sketch, "E28.3.6.3", {"start": v(112.3, 8.22) * mm, "end": v(105.36, 15.42) * mm});
            skLineSegment(sketch, "E28.direction1", {"start": v(52.85, 117.72) * mm, "end": v(69.85, 117.72) * mm, "construction": true});
            skLineSegment(sketch, "E28.direction2", {"start": v(52.85, 117.72) * mm, "end": v(52.85, 100.72) * mm, "construction": true});
            skSolve(sketch);
        }
        {
            var Q0;
            Q0 = qSketchRegion(id + "F2", true);
            var Q1;
            Q1 = qSketchRegion(id + "F3", true);
            extrude(context, id + "F4", {"entities" : qUnion([Q0, Q1]), "operationType" : NewBodyOperationType.REMOVE, "endBound" : BoundingType.SYMMETRIC, "oppositeDirection" : true, "depth" : 150 * mm, "offsetDistance" : 25 * mm});
        }
        {
            var Q0;
            Q0=makeQuery(id+"F1.opExtrude","SWEPT_FACE",FACE,{"disambiguationData":[OSD([sQuery(id+"F0.wireOp",EDGE,"E6.right")])]});
            var sketch = newSketch(context, id + "F5", { "sketchPlane" : qUnion([Q0])});
            skLineSegment(sketch, "E29", {"start": v(3.94, 117.42) * mm, "end": v(40.94, 117.42) * mm, "construction": true});
            skLineSegment(sketch, "E30", {"start": v(13.88, 124.62) * mm, "end": v(20.82, 117.42) * mm});
            skLineSegment(sketch, "E31", {"start": v(20.82, 117.42) * mm, "end": v(13.88, 110.22) * mm});
            skLineSegment(sketch, "E32", {"start": v(13.88, 110.22) * mm, "end": v(6.94, 117.42) * mm});
            skLineSegment(sketch, "E33", {"start": v(6.94, 117.42) * mm, "end": v(13.88, 124.62) * mm});
            skLineSegment(sketch, "E34.0.1.0", {"start": v(6.86, 100.42) * mm, "end": v(13.8, 107.62) * mm});
            skLineSegment(sketch, "E34.0.1.1", {"start": v(13.8, 93.22) * mm, "end": v(6.86, 100.42) * mm});
            skLineSegment(sketch, "E34.0.1.2", {"start": v(20.74, 100.42) * mm, "end": v(13.8, 93.22) * mm});
            skLineSegment(sketch, "E34.0.1.3", {"start": v(13.8, 107.62) * mm, "end": v(20.74, 100.42) * mm});
            skLineSegment(sketch, "E34.0.2.0", {"start": v(6.78, 83.42) * mm, "end": v(13.72, 90.62) * mm});
            skLineSegment(sketch, "E34.0.2.1", {"start": v(13.72, 76.22) * mm, "end": v(6.78, 83.42) * mm});
            skLineSegment(sketch, "E34.0.2.2", {"start": v(20.66, 83.42) * mm, "end": v(13.72, 76.22) * mm});
            skLineSegment(sketch, "E34.0.2.3", {"start": v(13.72, 90.62) * mm, "end": v(20.66, 83.42) * mm});
            skLineSegment(sketch, "E34.0.3.0", {"start": v(6.7, 66.42) * mm, "end": v(13.63, 73.62) * mm});
            skLineSegment(sketch, "E34.0.3.1", {"start": v(13.63, 59.22) * mm, "end": v(6.7, 66.42) * mm});
            skLineSegment(sketch, "E34.0.3.2", {"start": v(20.57, 66.42) * mm, "end": v(13.63, 59.22) * mm});
            skLineSegment(sketch, "E34.0.3.3", {"start": v(13.63, 73.62) * mm, "end": v(20.57, 66.42) * mm});
            skLineSegment(sketch, "E34.0.4.0", {"start": v(6.6, 49.42) * mm, "end": v(13.55, 56.62) * mm});
            skLineSegment(sketch, "E34.0.4.1", {"start": v(13.55, 42.22) * mm, "end": v(6.6, 49.42) * mm});
            skLineSegment(sketch, "E34.0.4.2", {"start": v(20.49, 49.42) * mm, "end": v(13.55, 42.22) * mm});
            skLineSegment(sketch, "E34.0.4.3", {"start": v(13.55, 56.62) * mm, "end": v(20.49, 49.42) * mm});
            skLineSegment(sketch, "E34.0.5.0", {"start": v(6.53, 32.42) * mm, "end": v(13.47, 39.62) * mm});
            skLineSegment(sketch, "E34.0.5.1", {"start": v(13.47, 25.22) * mm, "end": v(6.53, 32.42) * mm});
            skLineSegment(sketch, "E34.0.5.2", {"start": v(20.4, 32.42) * mm, "end": v(13.47, 25.22) * mm});
            skLineSegment(sketch, "E34.0.5.3", {"start": v(13.47, 39.62) * mm, "end": v(20.4, 32.42) * mm});
            skLineSegment(sketch, "E34.0.6.0", {"start": v(6.44, 15.42) * mm, "end": v(13.38, 22.62) * mm});
            skLineSegment(sketch, "E34.0.6.1", {"start": v(13.38, 8.22) * mm, "end": v(6.44, 15.42) * mm});
            skLineSegment(sketch, "E34.0.6.2", {"start": v(20.32, 15.42) * mm, "end": v(13.38, 8.22) * mm});
            skLineSegment(sketch, "E34.0.6.3", {"start": v(13.38, 22.62) * mm, "end": v(20.32, 15.42) * mm});
            skLineSegment(sketch, "E34.1.0.0", {"start": v(23.94, 117.42) * mm, "end": v(30.88, 124.62) * mm});
            skLineSegment(sketch, "E34.1.0.1", {"start": v(30.88, 110.22) * mm, "end": v(23.94, 117.42) * mm});
            skLineSegment(sketch, "E34.1.0.2", {"start": v(37.82, 117.42) * mm, "end": v(30.88, 110.22) * mm});
            skLineSegment(sketch, "E34.1.0.3", {"start": v(30.88, 124.62) * mm, "end": v(37.82, 117.42) * mm});
            skLineSegment(sketch, "E34.1.1.0", {"start": v(23.86, 100.42) * mm, "end": v(30.8, 107.62) * mm});
            skLineSegment(sketch, "E34.1.1.1", {"start": v(30.8, 93.22) * mm, "end": v(23.86, 100.42) * mm});
            skLineSegment(sketch, "E34.1.1.2", {"start": v(37.74, 100.42) * mm, "end": v(30.8, 93.22) * mm});
            skLineSegment(sketch, "E34.1.1.3", {"start": v(30.8, 107.62) * mm, "end": v(37.74, 100.42) * mm});
            skLineSegment(sketch, "E34.1.2.0", {"start": v(23.78, 83.42) * mm, "end": v(30.72, 90.62) * mm});
            skLineSegment(sketch, "E34.1.2.1", {"start": v(30.72, 76.22) * mm, "end": v(23.78, 83.42) * mm});
            skLineSegment(sketch, "E34.1.2.2", {"start": v(37.66, 83.42) * mm, "end": v(30.72, 76.22) * mm});
            skLineSegment(sketch, "E34.1.2.3", {"start": v(30.72, 90.62) * mm, "end": v(37.66, 83.42) * mm});
            skLineSegment(sketch, "E34.1.3.0", {"start": v(23.7, 66.42) * mm, "end": v(30.63, 73.62) * mm});
            skLineSegment(sketch, "E34.1.3.1", {"start": v(30.63, 59.22) * mm, "end": v(23.7, 66.42) * mm});
            skLineSegment(sketch, "E34.1.3.2", {"start": v(37.57, 66.42) * mm, "end": v(30.63, 59.22) * mm});
            skLineSegment(sketch, "E34.1.3.3", {"start": v(30.63, 73.62) * mm, "end": v(37.57, 66.42) * mm});
            skLineSegment(sketch, "E34.1.4.0", {"start": v(23.6, 49.42) * mm, "end": v(30.55, 56.62) * mm});
            skLineSegment(sketch, "E34.1.4.1", {"start": v(30.55, 42.22) * mm, "end": v(23.6, 49.42) * mm});
            skLineSegment(sketch, "E34.1.4.2", {"start": v(37.49, 49.42) * mm, "end": v(30.55, 42.22) * mm});
            skLineSegment(sketch, "E34.1.4.3", {"start": v(30.55, 56.62) * mm, "end": v(37.49, 49.42) * mm});
            skLineSegment(sketch, "E34.1.5.0", {"start": v(23.53, 32.42) * mm, "end": v(30.47, 39.62) * mm});
            skLineSegment(sketch, "E34.1.5.1", {"start": v(30.47, 25.22) * mm, "end": v(23.53, 32.42) * mm});
            skLineSegment(sketch, "E34.1.5.2", {"start": v(37.4, 32.42) * mm, "end": v(30.47, 25.22) * mm});
            skLineSegment(sketch, "E34.1.5.3", {"start": v(30.47, 39.62) * mm, "end": v(37.4, 32.42) * mm});
            skLineSegment(sketch, "E34.1.6.0", {"start": v(23.44, 15.42) * mm, "end": v(30.38, 22.62) * mm});
            skLineSegment(sketch, "E34.1.6.1", {"start": v(30.38, 8.22) * mm, "end": v(23.44, 15.42) * mm});
            skLineSegment(sketch, "E34.1.6.2", {"start": v(37.32, 15.42) * mm, "end": v(30.38, 8.22) * mm});
            skLineSegment(sketch, "E34.1.6.3", {"start": v(30.38, 22.62) * mm, "end": v(37.32, 15.42) * mm});
            skLineSegment(sketch, "E34.direction1", {"start": v(6.94, 117.42) * mm, "end": v(23.94, 117.42) * mm, "construction": true});
            skLineSegment(sketch, "E34.direction2", {"start": v(6.94, 117.42) * mm, "end": v(6.86, 100.42) * mm, "construction": true});
            skSolve(sketch);
        }
        {
            var Q0;
            Q0 = qSketchRegion(id + "F5", true);
            extrude(context, id + "F6", {"entities" : qUnion([Q0]), "operationType" : NewBodyOperationType.REMOVE, "oppositeDirection" : true, "depth" : 133.6 * mm, "offsetDistance" : 25 * mm});
        }
        {
            var Q0;
            Q0=makeQuery(id+"F1.opExtrude","SWEPT_FACE",FACE,{"disambiguationData":[OSD([sQuery(id+"F0.wireOp",EDGE,"E9")])]});
            var sketch = newSketch(context, id + "F7", { "sketchPlane" : qUnion([Q0])});
            skLineSegment(sketch, "E35.0", {"start": v(-24.75, 118) * mm, "end": v(-30.84, 124.62) * mm});
            skLineSegment(sketch, "E36.0", {"start": v(-30.84, 111.38) * mm, "end": v(-24.75, 118) * mm});
            skLineSegment(sketch, "E37.0", {"start": v(-36.94, 118) * mm, "end": v(-30.84, 111.38) * mm});
            skLineSegment(sketch, "E38.0", {"start": v(-30.84, 124.62) * mm, "end": v(-36.94, 118) * mm});
            skLineSegment(sketch, "E39", {"start": v(-40.94, 118) * mm, "end": v(7.76, 118) * mm, "construction": true});
            skLineSegment(sketch, "E40.direction1", {"start": v(-35, 118) * mm, "end": v(-18.9, 118) * mm, "construction": true});
            skLineSegment(sketch, "E41.0.1.0", {"start": v(-14.15, 124.62) * mm, "end": v(-20.25, 118) * mm});
            skLineSegment(sketch, "E41.3.1.0", {"start": v(-20.25, 118) * mm, "end": v(-14.15, 111.38) * mm});
            skLineSegment(sketch, "E41.6.1.0", {"start": v(-14.15, 111.38) * mm, "end": v(-8.05, 118) * mm});
            skLineSegment(sketch, "E41.9.1.0", {"start": v(-8.05, 118) * mm, "end": v(-14.15, 124.62) * mm});
            skLineSegment(sketch, "E41.0.2.0", {"start": v(2.55, 124.62) * mm, "end": v(-3.55, 118) * mm});
            skLineSegment(sketch, "E41.3.2.0", {"start": v(-3.55, 118) * mm, "end": v(2.55, 111.38) * mm});
            skLineSegment(sketch, "E41.6.2.0", {"start": v(2.55, 111.38) * mm, "end": v(8.65, 118) * mm});
            skLineSegment(sketch, "E41.9.2.0", {"start": v(8.65, 118) * mm, "end": v(2.55, 124.62) * mm});
            skLineSegment(sketch, "E42.0.1.0", {"start": v(-40.94, 101) * mm, "end": v(7.76, 101) * mm, "construction": true});
            skLineSegment(sketch, "E42.0.1.1", {"start": v(-24.75, 101) * mm, "end": v(-30.84, 107.62) * mm});
            skLineSegment(sketch, "E42.0.1.2", {"start": v(-30.84, 107.62) * mm, "end": v(-36.94, 101) * mm});
            skLineSegment(sketch, "E42.0.1.3", {"start": v(-36.94, 101) * mm, "end": v(-30.84, 94.38) * mm});
            skLineSegment(sketch, "E42.0.1.4", {"start": v(-30.84, 94.38) * mm, "end": v(-24.75, 101) * mm});
            skLineSegment(sketch, "E42.0.1.5", {"start": v(-35, 101) * mm, "end": v(-18.9, 101) * mm, "construction": true});
            skLineSegment(sketch, "E42.0.2.0", {"start": v(-40.94, 84) * mm, "end": v(7.76, 84) * mm, "construction": true});
            skLineSegment(sketch, "E42.0.2.1", {"start": v(-24.75, 84) * mm, "end": v(-30.84, 90.62) * mm});
            skLineSegment(sketch, "E42.0.2.2", {"start": v(-30.84, 90.62) * mm, "end": v(-36.94, 84) * mm});
            skLineSegment(sketch, "E42.0.2.3", {"start": v(-36.94, 84) * mm, "end": v(-30.84, 77.38) * mm});
            skLineSegment(sketch, "E42.0.2.4", {"start": v(-30.84, 77.38) * mm, "end": v(-24.75, 84) * mm});
            skLineSegment(sketch, "E42.0.2.5", {"start": v(-35, 84) * mm, "end": v(-18.9, 84) * mm, "construction": true});
            skLineSegment(sketch, "E42.0.3.0", {"start": v(-40.94, 67) * mm, "end": v(7.76, 67) * mm, "construction": true});
            skLineSegment(sketch, "E42.0.3.1", {"start": v(-24.75, 67) * mm, "end": v(-30.84, 73.62) * mm});
            skLineSegment(sketch, "E42.0.3.2", {"start": v(-30.84, 73.62) * mm, "end": v(-36.94, 67) * mm});
            skLineSegment(sketch, "E42.0.3.3", {"start": v(-36.94, 67) * mm, "end": v(-30.84, 60.38) * mm});
            skLineSegment(sketch, "E42.0.3.4", {"start": v(-30.84, 60.38) * mm, "end": v(-24.75, 67) * mm});
            skLineSegment(sketch, "E42.0.3.5", {"start": v(-35, 67) * mm, "end": v(-18.9, 67) * mm, "construction": true});
            skLineSegment(sketch, "E42.0.4.0", {"start": v(-40.94, 50) * mm, "end": v(7.76, 50) * mm, "construction": true});
            skLineSegment(sketch, "E42.0.4.1", {"start": v(-24.75, 50) * mm, "end": v(-30.84, 56.62) * mm});
            skLineSegment(sketch, "E42.0.4.2", {"start": v(-30.84, 56.62) * mm, "end": v(-36.94, 50) * mm});
            skLineSegment(sketch, "E42.0.4.3", {"start": v(-36.94, 50) * mm, "end": v(-30.84, 43.38) * mm});
            skLineSegment(sketch, "E42.0.4.4", {"start": v(-30.84, 43.38) * mm, "end": v(-24.75, 50) * mm});
            skLineSegment(sketch, "E42.0.4.5", {"start": v(-35, 50) * mm, "end": v(-18.9, 50) * mm, "construction": true});
            skLineSegment(sketch, "E42.0.5.0", {"start": v(-40.94, 33) * mm, "end": v(7.76, 33) * mm, "construction": true});
            skLineSegment(sketch, "E42.0.5.1", {"start": v(-24.75, 33) * mm, "end": v(-30.84, 39.62) * mm});
            skLineSegment(sketch, "E42.0.5.2", {"start": v(-30.84, 39.62) * mm, "end": v(-36.94, 33) * mm});
            skLineSegment(sketch, "E42.0.5.3", {"start": v(-36.94, 33) * mm, "end": v(-30.84, 26.38) * mm});
            skLineSegment(sketch, "E42.0.5.4", {"start": v(-30.84, 26.38) * mm, "end": v(-24.75, 33) * mm});
            skLineSegment(sketch, "E42.0.5.5", {"start": v(-35, 33) * mm, "end": v(-18.9, 33) * mm, "construction": true});
            skLineSegment(sketch, "E42.0.6.0", {"start": v(-40.94, 16) * mm, "end": v(7.76, 16) * mm, "construction": true});
            skLineSegment(sketch, "E42.0.6.1", {"start": v(-24.75, 16) * mm, "end": v(-30.84, 22.62) * mm});
            skLineSegment(sketch, "E42.0.6.2", {"start": v(-30.84, 22.62) * mm, "end": v(-36.94, 16) * mm});
            skLineSegment(sketch, "E42.0.6.3", {"start": v(-36.94, 16) * mm, "end": v(-30.84, 9.38) * mm});
            skLineSegment(sketch, "E42.0.6.4", {"start": v(-30.84, 9.38) * mm, "end": v(-24.75, 16) * mm});
            skLineSegment(sketch, "E42.0.6.5", {"start": v(-35, 16) * mm, "end": v(-18.9, 16) * mm, "construction": true});
            skLineSegment(sketch, "E42.direction1", {"start": v(-40.94, 118) * mm, "end": v(-15, 118) * mm, "construction": true});
            skLineSegment(sketch, "E42.direction2", {"start": v(-40.94, 118) * mm, "end": v(-40.94, 101) * mm, "construction": true});
            skLineSegment(sketch, "E43.0.1.0", {"start": v(-20.25, 101) * mm, "end": v(-14.15, 94.38) * mm});
            skLineSegment(sketch, "E43.0.1.1", {"start": v(-14.15, 107.62) * mm, "end": v(-20.25, 101) * mm});
            skLineSegment(sketch, "E43.0.1.2", {"start": v(-8.05, 101) * mm, "end": v(-14.15, 107.62) * mm});
            skLineSegment(sketch, "E43.0.1.3", {"start": v(-14.15, 94.38) * mm, "end": v(-8.05, 101) * mm});
            skLineSegment(sketch, "E43.0.1.4", {"start": v(-3.55, 101) * mm, "end": v(2.55, 94.38) * mm});
            skLineSegment(sketch, "E43.0.1.5", {"start": v(2.55, 107.62) * mm, "end": v(-3.55, 101) * mm});
            skLineSegment(sketch, "E43.0.1.6", {"start": v(8.65, 101) * mm, "end": v(2.55, 107.62) * mm});
            skLineSegment(sketch, "E43.0.1.7", {"start": v(2.55, 94.38) * mm, "end": v(8.65, 101) * mm});
            skLineSegment(sketch, "E43.0.2.0", {"start": v(-20.25, 84) * mm, "end": v(-14.15, 77.38) * mm});
            skLineSegment(sketch, "E43.0.2.1", {"start": v(-14.15, 90.62) * mm, "end": v(-20.25, 84) * mm});
            skLineSegment(sketch, "E43.0.2.2", {"start": v(-8.05, 84) * mm, "end": v(-14.15, 90.62) * mm});
            skLineSegment(sketch, "E43.0.2.3", {"start": v(-14.15, 77.38) * mm, "end": v(-8.05, 84) * mm});
            skLineSegment(sketch, "E43.0.2.4", {"start": v(-3.55, 84) * mm, "end": v(2.55, 77.38) * mm});
            skLineSegment(sketch, "E43.0.2.5", {"start": v(2.55, 90.62) * mm, "end": v(-3.55, 84) * mm});
            skLineSegment(sketch, "E43.0.2.6", {"start": v(8.65, 84) * mm, "end": v(2.55, 90.62) * mm});
            skLineSegment(sketch, "E43.0.2.7", {"start": v(2.55, 77.38) * mm, "end": v(8.65, 84) * mm});
            skLineSegment(sketch, "E43.0.3.0", {"start": v(-20.25, 67) * mm, "end": v(-14.15, 60.38) * mm});
            skLineSegment(sketch, "E43.0.3.1", {"start": v(-14.15, 73.62) * mm, "end": v(-20.25, 67) * mm});
            skLineSegment(sketch, "E43.0.3.2", {"start": v(-8.05, 67) * mm, "end": v(-14.15, 73.62) * mm});
            skLineSegment(sketch, "E43.0.3.3", {"start": v(-14.15, 60.38) * mm, "end": v(-8.05, 67) * mm});
            skLineSegment(sketch, "E43.0.3.4", {"start": v(-3.55, 67) * mm, "end": v(2.55, 60.38) * mm});
            skLineSegment(sketch, "E43.0.3.5", {"start": v(2.55, 73.62) * mm, "end": v(-3.55, 67) * mm});
            skLineSegment(sketch, "E43.0.3.6", {"start": v(8.65, 67) * mm, "end": v(2.55, 73.62) * mm});
            skLineSegment(sketch, "E43.0.3.7", {"start": v(2.55, 60.38) * mm, "end": v(8.65, 67) * mm});
            skLineSegment(sketch, "E43.0.4.0", {"start": v(-20.25, 50) * mm, "end": v(-14.15, 43.38) * mm});
            skLineSegment(sketch, "E43.0.4.1", {"start": v(-14.15, 56.62) * mm, "end": v(-20.25, 50) * mm});
            skLineSegment(sketch, "E43.0.4.2", {"start": v(-8.05, 50) * mm, "end": v(-14.15, 56.62) * mm});
            skLineSegment(sketch, "E43.0.4.3", {"start": v(-14.15, 43.38) * mm, "end": v(-8.05, 50) * mm});
            skLineSegment(sketch, "E43.0.4.4", {"start": v(-3.55, 50) * mm, "end": v(2.55, 43.38) * mm});
            skLineSegment(sketch, "E43.0.4.5", {"start": v(2.55, 56.62) * mm, "end": v(-3.55, 50) * mm});
            skLineSegment(sketch, "E43.0.4.6", {"start": v(8.65, 50) * mm, "end": v(2.55, 56.62) * mm});
            skLineSegment(sketch, "E43.0.4.7", {"start": v(2.55, 43.38) * mm, "end": v(8.65, 50) * mm});
            skLineSegment(sketch, "E43.0.5.0", {"start": v(-20.25, 33) * mm, "end": v(-14.15, 26.38) * mm});
            skLineSegment(sketch, "E43.0.5.1", {"start": v(-14.15, 39.62) * mm, "end": v(-20.25, 33) * mm});
            skLineSegment(sketch, "E43.0.5.2", {"start": v(-8.05, 33) * mm, "end": v(-14.15, 39.62) * mm});
            skLineSegment(sketch, "E43.0.5.3", {"start": v(-14.15, 26.38) * mm, "end": v(-8.05, 33) * mm});
            skLineSegment(sketch, "E43.0.5.4", {"start": v(-3.55, 33) * mm, "end": v(2.55, 26.38) * mm});
            skLineSegment(sketch, "E43.0.5.5", {"start": v(2.55, 39.62) * mm, "end": v(-3.55, 33) * mm});
            skLineSegment(sketch, "E43.0.5.6", {"start": v(8.65, 33) * mm, "end": v(2.55, 39.62) * mm});
            skLineSegment(sketch, "E43.0.5.7", {"start": v(2.55, 26.38) * mm, "end": v(8.65, 33) * mm});
            skLineSegment(sketch, "E43.0.6.0", {"start": v(-20.25, 16) * mm, "end": v(-14.15, 9.38) * mm});
            skLineSegment(sketch, "E43.0.6.1", {"start": v(-14.15, 22.62) * mm, "end": v(-20.25, 16) * mm});
            skLineSegment(sketch, "E43.0.6.2", {"start": v(-8.05, 16) * mm, "end": v(-14.15, 22.62) * mm});
            skLineSegment(sketch, "E43.0.6.3", {"start": v(-14.15, 9.38) * mm, "end": v(-8.05, 16) * mm});
            skLineSegment(sketch, "E43.0.6.4", {"start": v(-3.55, 16) * mm, "end": v(2.55, 9.38) * mm});
            skLineSegment(sketch, "E43.0.6.5", {"start": v(2.55, 22.62) * mm, "end": v(-3.55, 16) * mm});
            skLineSegment(sketch, "E43.0.6.6", {"start": v(8.65, 16) * mm, "end": v(2.55, 22.62) * mm});
            skLineSegment(sketch, "E43.0.6.7", {"start": v(2.55, 9.38) * mm, "end": v(8.65, 16) * mm});
            skLineSegment(sketch, "E43.direction1", {"start": v(-14.15, 111.38) * mm, "end": v(11.73, 111.38) * mm, "construction": true});
            skLineSegment(sketch, "E43.direction2", {"start": v(-14.15, 111.38) * mm, "end": v(-14.15, 94.38) * mm, "construction": true});
            skSolve(sketch);
        }
        {
            var Q0;
            Q0 = qSketchRegion(id + "F7", true);
            extrude(context, id + "F8", {"entities" : qUnion([Q0]), "operationType" : NewBodyOperationType.REMOVE, "oppositeDirection" : true, "depth" : 25 * mm, "offsetDistance" : 25 * mm});
        }
        {
            var Q0;
            Q0=makeQuery(id+"F1.opExtrude","CAP_FACE",FACE,{"disambiguationData":[OSD([sQuery(id+"F0.wireOp",EDGE,"E0.top"),sQuery(id+"F0.wireOp",EDGE,"E3.top"),sQuery(id+"F0.wireOp",EDGE,"E1"),sQuery(id+"F0.wireOp",EDGE,"E4"),sQuery(id+"F0.wireOp",EDGE,"E5"),sQuery(id+"F0.wireOp",EDGE,"E6.bottom"),sQuery(id+"F0.wireOp",EDGE,"E6.top"),sQuery(id+"F0.wireOp",EDGE,"E6.right"),sQuery(id+"F0.wireOp",EDGE,"E8"),sQuery(id+"F0.wireOp",EDGE,"E9"),sQuery(id+"F0.wireOp",EDGE,"E10"),sQuery(id+"F0.wireOp",EDGE,"E11.bottom"),sQuery(id+"F0.wireOp",EDGE,"E11.top"),sQuery(id+"F0.wireOp",EDGE,"E11.left"),sQuery(id+"F0.wireOp",EDGE,"E11.right")])],"isStart":true});
            var sketch = newSketch(context, id + "F9", { "sketchPlane" : qUnion([Q0])});
            skLineSegment(sketch, "E44.0", {"start": v(-50.64, 7.76) * mm, "end": v(49.36, 7.76) * mm});
            skLineSegment(sketch, "E45.0", {"start": v(-50.64, -40.94) * mm, "end": v(-50.64, 7.76) * mm});
            skLineSegment(sketch, "E46.0", {"start": v(-50.64, -40.94) * mm, "end": v(124.36, -40.94) * mm});
            skLineSegment(sketch, "E47.0", {"start": v(124.36, -40.94) * mm, "end": v(124.36, -3.94) * mm});
            skLineSegment(sketch, "E48.0", {"start": v(49.36, -3.94) * mm, "end": v(124.36, -3.94) * mm});
            skLineSegment(sketch, "E49.0", {"start": v(49.36, -3.94) * mm, "end": v(49.36, 7.76) * mm});
            skSolve(sketch);
        }
        {
            var Q0;
            Q0 = qSketchRegion(id + "F9", true);
            extrude(context, id + "F10", {"entities" : qUnion([Q0]), "operationType" : NewBodyOperationType.ADD, "oppositeDirection" : true, "depth" : 2.1 * mm, "offsetDistance" : 25 * mm});
        }
        {
            var Q0;
            Q0=makeQuery(id+"F10.boolean.opBoolean","MERGE",FACE,{"derivedFrom":[makeQuery(id+"F1.opExtrude","CAP_FACE",FACE,{"disambiguationData":[OSD([sQuery(id+"F0.wireOp",EDGE,"E0.top"),sQuery(id+"F0.wireOp",EDGE,"E3.top"),sQuery(id+"F0.wireOp",EDGE,"E1"),sQuery(id+"F0.wireOp",EDGE,"E4"),sQuery(id+"F0.wireOp",EDGE,"E5"),sQuery(id+"F0.wireOp",EDGE,"E6.bottom"),sQuery(id+"F0.wireOp",EDGE,"E6.top"),sQuery(id+"F0.wireOp",EDGE,"E6.right"),sQuery(id+"F0.wireOp",EDGE,"E8"),sQuery(id+"F0.wireOp",EDGE,"E9"),sQuery(id+"F0.wireOp",EDGE,"E10"),sQuery(id+"F0.wireOp",EDGE,"E11.bottom"),sQuery(id+"F0.wireOp",EDGE,"E11.top"),sQuery(id+"F0.wireOp",EDGE,"E11.left"),sQuery(id+"F0.wireOp",EDGE,"E11.right")])],"isStart":true}),makeQuery(id+"F10.opExtrude","CAP_FACE",FACE,{"disambiguationData":[OSD([sQuery(id+"F9.wireOp",EDGE,"E44.0"),sQuery(id+"F9.wireOp",EDGE,"E45.0"),sQuery(id+"F9.wireOp",EDGE,"E46.0"),sQuery(id+"F9.wireOp",EDGE,"E47.0"),sQuery(id+"F9.wireOp",EDGE,"E48.0"),sQuery(id+"F9.wireOp",EDGE,"E49.0")])],"isStart":true})]});
            var sketch = newSketch(context, id + "F11", { "sketchPlane" : qUnion([Q0])});
            skLineSegment(sketch, "E50", {"start": v(-40.4, 4.66) * mm, "end": v(-33.56, -1.2) * mm});
            skLineSegment(sketch, "E51", {"start": v(-33.56, -1.2) * mm, "end": v(-40.4, -7.04) * mm});
            skLineSegment(sketch, "E52", {"start": v(-40.4, -7.04) * mm, "end": v(-47.24, -1.2) * mm});
            skLineSegment(sketch, "E53", {"start": v(-47.24, -1.2) * mm, "end": v(-40.4, 4.66) * mm});
            skLineSegment(sketch, "E54.0.1.0", {"start": v(-47.24, -16.2) * mm, "end": v(-40.4, -10.34) * mm});
            skLineSegment(sketch, "E54.0.1.1", {"start": v(-40.4, -22.04) * mm, "end": v(-47.24, -16.2) * mm});
            skLineSegment(sketch, "E54.0.1.2", {"start": v(-33.56, -16.2) * mm, "end": v(-40.4, -22.04) * mm});
            skLineSegment(sketch, "E54.0.1.3", {"start": v(-40.4, -10.34) * mm, "end": v(-33.56, -16.2) * mm});
            skLineSegment(sketch, "E54.0.2.0", {"start": v(-47.24, -31.2) * mm, "end": v(-40.4, -25.34) * mm});
            skLineSegment(sketch, "E54.0.2.1", {"start": v(-40.4, -37.04) * mm, "end": v(-47.24, -31.2) * mm});
            skLineSegment(sketch, "E54.0.2.2", {"start": v(-33.56, -31.2) * mm, "end": v(-40.4, -37.04) * mm});
            skLineSegment(sketch, "E54.0.2.3", {"start": v(-40.4, -25.34) * mm, "end": v(-33.56, -31.2) * mm});
            skLineSegment(sketch, "E54.1.0.0", {"start": v(-22.24, -1.2) * mm, "end": v(-15.4, 4.66) * mm});
            skLineSegment(sketch, "E54.1.0.1", {"start": v(-15.4, -7.04) * mm, "end": v(-22.24, -1.2) * mm});
            skLineSegment(sketch, "E54.1.0.2", {"start": v(-8.56, -1.2) * mm, "end": v(-15.4, -7.04) * mm});
            skLineSegment(sketch, "E54.1.0.3", {"start": v(-15.4, 4.66) * mm, "end": v(-8.56, -1.2) * mm});
            skLineSegment(sketch, "E54.1.1.0", {"start": v(-22.24, -16.2) * mm, "end": v(-15.4, -10.34) * mm});
            skLineSegment(sketch, "E54.1.1.1", {"start": v(-15.4, -22.04) * mm, "end": v(-22.24, -16.2) * mm});
            skLineSegment(sketch, "E54.1.1.2", {"start": v(-8.56, -16.2) * mm, "end": v(-15.4, -22.04) * mm});
            skLineSegment(sketch, "E54.1.1.3", {"start": v(-15.4, -10.34) * mm, "end": v(-8.56, -16.2) * mm});
            skLineSegment(sketch, "E54.1.2.0", {"start": v(-22.24, -31.2) * mm, "end": v(-15.4, -25.34) * mm});
            skLineSegment(sketch, "E54.1.2.1", {"start": v(-15.4, -37.04) * mm, "end": v(-22.24, -31.2) * mm});
            skLineSegment(sketch, "E54.1.2.2", {"start": v(-8.56, -31.2) * mm, "end": v(-15.4, -37.04) * mm});
            skLineSegment(sketch, "E54.1.2.3", {"start": v(-15.4, -25.34) * mm, "end": v(-8.56, -31.2) * mm});
            skLineSegment(sketch, "E54.2.0.0", {"start": v(2.76, -1.2) * mm, "end": v(9.6, 4.66) * mm});
            skLineSegment(sketch, "E54.2.0.1", {"start": v(9.6, -7.04) * mm, "end": v(2.76, -1.2) * mm});
            skLineSegment(sketch, "E54.2.0.2", {"start": v(16.44, -1.2) * mm, "end": v(9.6, -7.04) * mm});
            skLineSegment(sketch, "E54.2.0.3", {"start": v(9.6, 4.66) * mm, "end": v(16.44, -1.2) * mm});
            skLineSegment(sketch, "E54.2.1.0", {"start": v(2.76, -16.2) * mm, "end": v(9.6, -10.34) * mm});
            skLineSegment(sketch, "E54.2.1.1", {"start": v(9.6, -22.04) * mm, "end": v(2.76, -16.2) * mm});
            skLineSegment(sketch, "E54.2.1.2", {"start": v(16.44, -16.2) * mm, "end": v(9.6, -22.04) * mm});
            skLineSegment(sketch, "E54.2.1.3", {"start": v(9.6, -10.34) * mm, "end": v(16.44, -16.2) * mm});
            skLineSegment(sketch, "E54.2.2.0", {"start": v(2.76, -31.2) * mm, "end": v(9.6, -25.34) * mm});
            skLineSegment(sketch, "E54.2.2.1", {"start": v(9.6, -37.04) * mm, "end": v(2.76, -31.2) * mm});
            skLineSegment(sketch, "E54.2.2.2", {"start": v(16.44, -31.2) * mm, "end": v(9.6, -37.04) * mm});
            skLineSegment(sketch, "E54.2.2.3", {"start": v(9.6, -25.34) * mm, "end": v(16.44, -31.2) * mm});
            skLineSegment(sketch, "E54.3.0.0", {"start": v(27.76, -1.2) * mm, "end": v(34.6, 4.66) * mm});
            skLineSegment(sketch, "E54.3.0.1", {"start": v(34.6, -7.04) * mm, "end": v(27.76, -1.2) * mm});
            skLineSegment(sketch, "E54.3.0.2", {"start": v(41.44, -1.2) * mm, "end": v(34.6, -7.04) * mm});
            skLineSegment(sketch, "E54.3.0.3", {"start": v(34.6, 4.66) * mm, "end": v(41.44, -1.2) * mm});
            skLineSegment(sketch, "E54.3.1.0", {"start": v(27.76, -16.2) * mm, "end": v(34.6, -10.34) * mm});
            skLineSegment(sketch, "E54.3.1.1", {"start": v(34.6, -22.04) * mm, "end": v(27.76, -16.2) * mm});
            skLineSegment(sketch, "E54.3.1.2", {"start": v(41.44, -16.2) * mm, "end": v(34.6, -22.04) * mm});
            skLineSegment(sketch, "E54.3.1.3", {"start": v(34.6, -10.34) * mm, "end": v(41.44, -16.2) * mm});
            skLineSegment(sketch, "E54.3.2.0", {"start": v(27.76, -31.2) * mm, "end": v(34.6, -25.34) * mm});
            skLineSegment(sketch, "E54.3.2.1", {"start": v(34.6, -37.04) * mm, "end": v(27.76, -31.2) * mm});
            skLineSegment(sketch, "E54.3.2.2", {"start": v(41.44, -31.2) * mm, "end": v(34.6, -37.04) * mm});
            skLineSegment(sketch, "E54.3.2.3", {"start": v(34.6, -25.34) * mm, "end": v(41.44, -31.2) * mm});
            skLineSegment(sketch, "E54.4.1.0", {"start": v(52.76, -16.2) * mm, "end": v(59.6, -10.34) * mm});
            skLineSegment(sketch, "E54.4.1.1", {"start": v(59.6, -22.04) * mm, "end": v(52.76, -16.2) * mm});
            skLineSegment(sketch, "E54.4.1.2", {"start": v(66.44, -16.2) * mm, "end": v(59.6, -22.04) * mm});
            skLineSegment(sketch, "E54.4.1.3", {"start": v(59.6, -10.34) * mm, "end": v(66.44, -16.2) * mm});
            skLineSegment(sketch, "E54.4.2.0", {"start": v(52.76, -31.2) * mm, "end": v(59.6, -25.34) * mm});
            skLineSegment(sketch, "E54.4.2.1", {"start": v(59.6, -37.04) * mm, "end": v(52.76, -31.2) * mm});
            skLineSegment(sketch, "E54.4.2.2", {"start": v(66.44, -31.2) * mm, "end": v(59.6, -37.04) * mm});
            skLineSegment(sketch, "E54.4.2.3", {"start": v(59.6, -25.34) * mm, "end": v(66.44, -31.2) * mm});
            skLineSegment(sketch, "E54.5.1.0", {"start": v(77.76, -16.2) * mm, "end": v(84.6, -10.34) * mm});
            skLineSegment(sketch, "E54.5.1.1", {"start": v(84.6, -22.04) * mm, "end": v(77.76, -16.2) * mm});
            skLineSegment(sketch, "E54.5.1.2", {"start": v(91.44, -16.2) * mm, "end": v(84.6, -22.04) * mm});
            skLineSegment(sketch, "E54.5.1.3", {"start": v(84.6, -10.34) * mm, "end": v(91.44, -16.2) * mm});
            skLineSegment(sketch, "E54.5.2.0", {"start": v(77.76, -31.2) * mm, "end": v(84.6, -25.34) * mm});
            skLineSegment(sketch, "E54.5.2.1", {"start": v(84.6, -37.04) * mm, "end": v(77.76, -31.2) * mm});
            skLineSegment(sketch, "E54.5.2.2", {"start": v(91.44, -31.2) * mm, "end": v(84.6, -37.04) * mm});
            skLineSegment(sketch, "E54.5.2.3", {"start": v(84.6, -25.34) * mm, "end": v(91.44, -31.2) * mm});
            skLineSegment(sketch, "E54.6.1.0", {"start": v(102.76, -16.2) * mm, "end": v(109.6, -10.34) * mm});
            skLineSegment(sketch, "E54.6.1.1", {"start": v(109.6, -22.04) * mm, "end": v(102.76, -16.2) * mm});
            skLineSegment(sketch, "E54.6.1.2", {"start": v(116.44, -16.2) * mm, "end": v(109.6, -22.04) * mm});
            skLineSegment(sketch, "E54.6.1.3", {"start": v(109.6, -10.34) * mm, "end": v(116.44, -16.2) * mm});
            skLineSegment(sketch, "E54.6.2.0", {"start": v(102.76, -31.2) * mm, "end": v(109.6, -25.34) * mm});
            skLineSegment(sketch, "E54.6.2.1", {"start": v(109.6, -37.04) * mm, "end": v(102.76, -31.2) * mm});
            skLineSegment(sketch, "E54.6.2.2", {"start": v(116.44, -31.2) * mm, "end": v(109.6, -37.04) * mm});
            skLineSegment(sketch, "E54.6.2.3", {"start": v(109.6, -25.34) * mm, "end": v(116.44, -31.2) * mm});
            skLineSegment(sketch, "E54.direction1", {"start": v(-47.24, -1.2) * mm, "end": v(-22.24, -1.2) * mm, "construction": true});
            skLineSegment(sketch, "E54.direction2", {"start": v(-47.24, -1.2) * mm, "end": v(-47.24, -16.2) * mm, "construction": true});
            skSolve(sketch);
        }
        {
            var Q0;
            Q0 = qSketchRegion(id + "F11", true);
            extrude(context, id + "F12", {"entities" : qUnion([Q0]), "operationType" : NewBodyOperationType.REMOVE, "oppositeDirection" : true, "depth" : 25 * mm, "offsetDistance" : 25 * mm});
        }
        {
            var Q0;
            Q0=qCreatedBy(makeId("Front.planeOp"),FACE);
            var sketch = newSketch(context, id + "F13", { "sketchPlane" : qUnion([Q0])});
            skLineSegment(sketch, "E55.bottom", {"start": v(-87.6, 150.48) * mm, "end": v(170.82, 150.48) * mm});
            skLineSegment(sketch, "E55.top", {"start": v(-87.6, 75.24) * mm, "end": v(170.82, 75.24) * mm});
            skLineSegment(sketch, "E55.left", {"start": v(-87.6, 150.48) * mm, "end": v(-87.6, 75.24) * mm});
            skLineSegment(sketch, "E55.right", {"start": v(170.82, 150.48) * mm, "end": v(170.82, 75.24) * mm});
            skSolve(sketch);
        }
        {
            var Q0;
            Q0=makeQuery(id+"F13.imprint","IMPRINT",FACE,{"disambiguationData":[TD([[makeQuery(id+"F13.imprint","IMPRINT",EDGE,{"derivedFrom":sQuery(id+"F13.wireOp",EDGE,"E55.bottom")}),-1.0]])]});
            extrude(context, id + "F14", {"entities" : qUnion([Q0]), "operationType" : NewBodyOperationType.REMOVE, "endBound" : BoundingType.THROUGH_ALL, "oppositeDirection" : true, "depth" : 60 * mm, "offsetDistance" : 25 * mm, "hasSecondDirection" : true, "secondDirectionOppositeDirection" : false, "secondDirectionDepth" : 25 * mm});
        }
        {
            var Q0;
            Q0=makeQuery(id+"F1.opExtrude","SWEPT_EDGE",EDGE,{"disambiguationData":[OSD([sQuery(id+"F0.wireOp",EDGE,"E6.top"),sQuery(id+"F0.wireOp",EDGE,"E10")])]});
            fillet(context, id + "F15", {"entities" : qUnion([Q0]), "radius" : 5 * mm, "tangentPropagation" : true, "allowEdgeOverflow" : false});
        }
        {
            var Q0;
            Q0=makeQuery(id+"F1.opExtrude","SWEPT_EDGE",EDGE,{"disambiguationData":[OSD([sQuery(id+"F0.wireOp",EDGE,"E11.right"),sQuery(id+"F0.wireOp",EDGE,"E14")])]});
            var Q1;
            Q1=makeQuery(id+"F1.opExtrude","SWEPT_EDGE",EDGE,{"disambiguationData":[OSD([sQuery(id+"F0.wireOp",EDGE,"E3.top"),sQuery(id+"F0.wireOp",EDGE,"E4")])]});
            var Q2;
            Q2=makeQuery(id+"F1.opExtrude","SWEPT_EDGE",EDGE,{"disambiguationData":[OSD([sQuery(id+"F0.wireOp",EDGE,"E3.top"),sQuery(id+"F0.wireOp",EDGE,"E5")])]});
            var Q3;
            Q3=makeQuery(id+"F1.opExtrude","SWEPT_EDGE",EDGE,{"disambiguationData":[OSD([sQuery(id+"F0.wireOp",EDGE,"E14"),sQuery(id+"F0.wireOp",EDGE,"E15")])]});
            var Q4;
            Q4=makeQuery(id+"F1.opExtrude","SWEPT_EDGE",EDGE,{"disambiguationData":[OSD([sQuery(id+"F0.wireOp",EDGE,"E11.top"),sQuery(id+"F0.wireOp",EDGE,"E11.right")])]});
            var Q5;
            Q5=makeQuery(id+"F1.opExtrude","SWEPT_EDGE",EDGE,{"disambiguationData":[OSD([sQuery(id+"F0.wireOp",EDGE,"E1"),sQuery(id+"F0.wireOp",EDGE,"E4")])]});
            var Q6;
            Q6=makeQuery(id+"F1.opExtrude","SWEPT_EDGE",EDGE,{"disambiguationData":[OSD([sQuery(id+"F0.wireOp",EDGE,"E11.top"),sQuery(id+"F0.wireOp",EDGE,"E15")])]});
            var Q7;
            Q7=makeQuery(id+"F1.opExtrude","SWEPT_EDGE",EDGE,{"disambiguationData":[OSD([sQuery(id+"F0.wireOp",EDGE,"E1"),sQuery(id+"F0.wireOp",EDGE,"E5")])]});
            var Q8;
            Q8=makeQuery(id+"F10.boolean.opBoolean","INTERSECT",EDGE,{"derivedFrom":[makeQuery(id+"F1.opExtrude","SWEPT_FACE",FACE,{"disambiguationData":[OSD([sQuery(id+"F0.wireOp",EDGE,"E5")])]}),makeQuery(id+"F10.opExtrude","CAP_FACE",FACE,{"disambiguationData":[OSD([sQuery(id+"F9.wireOp",EDGE,"E44.0"),sQuery(id+"F9.wireOp",EDGE,"E45.0"),sQuery(id+"F9.wireOp",EDGE,"E46.0"),sQuery(id+"F9.wireOp",EDGE,"E47.0"),sQuery(id+"F9.wireOp",EDGE,"E48.0"),sQuery(id+"F9.wireOp",EDGE,"E49.0")])],"isStart":false})]});
            var Q9;
            Q9=makeQuery(id+"F10.boolean.opBoolean","INTERSECT",EDGE,{"derivedFrom":[makeQuery(id+"F1.opExtrude","SWEPT_FACE",FACE,{"disambiguationData":[OSD([sQuery(id+"F0.wireOp",EDGE,"E4")])]}),makeQuery(id+"F10.opExtrude","CAP_FACE",FACE,{"disambiguationData":[OSD([sQuery(id+"F9.wireOp",EDGE,"E44.0"),sQuery(id+"F9.wireOp",EDGE,"E45.0"),sQuery(id+"F9.wireOp",EDGE,"E46.0"),sQuery(id+"F9.wireOp",EDGE,"E47.0"),sQuery(id+"F9.wireOp",EDGE,"E48.0"),sQuery(id+"F9.wireOp",EDGE,"E49.0")])],"isStart":false})]});
            var Q10;
            Q10=makeQuery(id+"F10.boolean.opBoolean","INTERSECT",EDGE,{"derivedFrom":[makeQuery(id+"F1.opExtrude","SWEPT_FACE",FACE,{"disambiguationData":[OSD([sQuery(id+"F0.wireOp",EDGE,"E3.top")])]}),makeQuery(id+"F10.opExtrude","CAP_FACE",FACE,{"disambiguationData":[OSD([sQuery(id+"F9.wireOp",EDGE,"E44.0"),sQuery(id+"F9.wireOp",EDGE,"E45.0"),sQuery(id+"F9.wireOp",EDGE,"E46.0"),sQuery(id+"F9.wireOp",EDGE,"E47.0"),sQuery(id+"F9.wireOp",EDGE,"E48.0"),sQuery(id+"F9.wireOp",EDGE,"E49.0")])],"isStart":false})]});
            var Q11;
            Q11=makeQuery(id+"F10.boolean.opBoolean","INTERSECT",EDGE,{"derivedFrom":[makeQuery(id+"F1.opExtrude","SWEPT_FACE",FACE,{"disambiguationData":[OSD([sQuery(id+"F0.wireOp",EDGE,"E1")])]}),makeQuery(id+"F10.opExtrude","CAP_FACE",FACE,{"disambiguationData":[OSD([sQuery(id+"F9.wireOp",EDGE,"E44.0"),sQuery(id+"F9.wireOp",EDGE,"E45.0"),sQuery(id+"F9.wireOp",EDGE,"E46.0"),sQuery(id+"F9.wireOp",EDGE,"E47.0"),sQuery(id+"F9.wireOp",EDGE,"E48.0"),sQuery(id+"F9.wireOp",EDGE,"E49.0")])],"isStart":false})]});
            var Q12;
            Q12=makeQuery(id+"F10.boolean.opBoolean","INTERSECT",EDGE,{"derivedFrom":[makeQuery(id+"F1.opExtrude","SWEPT_FACE",FACE,{"disambiguationData":[OSD([sQuery(id+"F0.wireOp",EDGE,"E11.top")])]}),makeQuery(id+"F10.opExtrude","CAP_FACE",FACE,{"disambiguationData":[OSD([sQuery(id+"F9.wireOp",EDGE,"E44.0"),sQuery(id+"F9.wireOp",EDGE,"E45.0"),sQuery(id+"F9.wireOp",EDGE,"E46.0"),sQuery(id+"F9.wireOp",EDGE,"E47.0"),sQuery(id+"F9.wireOp",EDGE,"E48.0"),sQuery(id+"F9.wireOp",EDGE,"E49.0")])],"isStart":false})]});
            var Q13;
            Q13=makeQuery(id+"F10.boolean.opBoolean","INTERSECT",EDGE,{"derivedFrom":[makeQuery(id+"F1.opExtrude","SWEPT_FACE",FACE,{"disambiguationData":[OSD([sQuery(id+"F0.wireOp",EDGE,"E14")])]}),makeQuery(id+"F10.opExtrude","CAP_FACE",FACE,{"disambiguationData":[OSD([sQuery(id+"F9.wireOp",EDGE,"E44.0"),sQuery(id+"F9.wireOp",EDGE,"E45.0"),sQuery(id+"F9.wireOp",EDGE,"E46.0"),sQuery(id+"F9.wireOp",EDGE,"E47.0"),sQuery(id+"F9.wireOp",EDGE,"E48.0"),sQuery(id+"F9.wireOp",EDGE,"E49.0")])],"isStart":false})]});
            var Q14;
            Q14=makeQuery(id+"F10.boolean.opBoolean","INTERSECT",EDGE,{"derivedFrom":[makeQuery(id+"F1.opExtrude","SWEPT_FACE",FACE,{"disambiguationData":[OSD([sQuery(id+"F0.wireOp",EDGE,"E15")])]}),makeQuery(id+"F10.opExtrude","CAP_FACE",FACE,{"disambiguationData":[OSD([sQuery(id+"F9.wireOp",EDGE,"E44.0"),sQuery(id+"F9.wireOp",EDGE,"E45.0"),sQuery(id+"F9.wireOp",EDGE,"E46.0"),sQuery(id+"F9.wireOp",EDGE,"E47.0"),sQuery(id+"F9.wireOp",EDGE,"E48.0"),sQuery(id+"F9.wireOp",EDGE,"E49.0")])],"isStart":false})]});
            var Q15;
            Q15=makeQuery(id+"F10.boolean.opBoolean","INTERSECT",EDGE,{"derivedFrom":[makeQuery(id+"F1.opExtrude","SWEPT_FACE",FACE,{"disambiguationData":[OSD([sQuery(id+"F0.wireOp",EDGE,"E11.right")])]}),makeQuery(id+"F10.opExtrude","CAP_FACE",FACE,{"disambiguationData":[OSD([sQuery(id+"F9.wireOp",EDGE,"E44.0"),sQuery(id+"F9.wireOp",EDGE,"E45.0"),sQuery(id+"F9.wireOp",EDGE,"E46.0"),sQuery(id+"F9.wireOp",EDGE,"E47.0"),sQuery(id+"F9.wireOp",EDGE,"E48.0"),sQuery(id+"F9.wireOp",EDGE,"E49.0")])],"isStart":false})]});
            fillet(context, id + "F16", {"entities" : qUnion([Q0, Q1, Q2, Q3, Q4, Q5, Q6, Q7, Q8, Q9, Q10, Q11, Q12, Q13, Q14, Q15]), "radius" : 2 * mm, "tangentPropagation" : true, "allowEdgeOverflow" : false});
        }
    });
